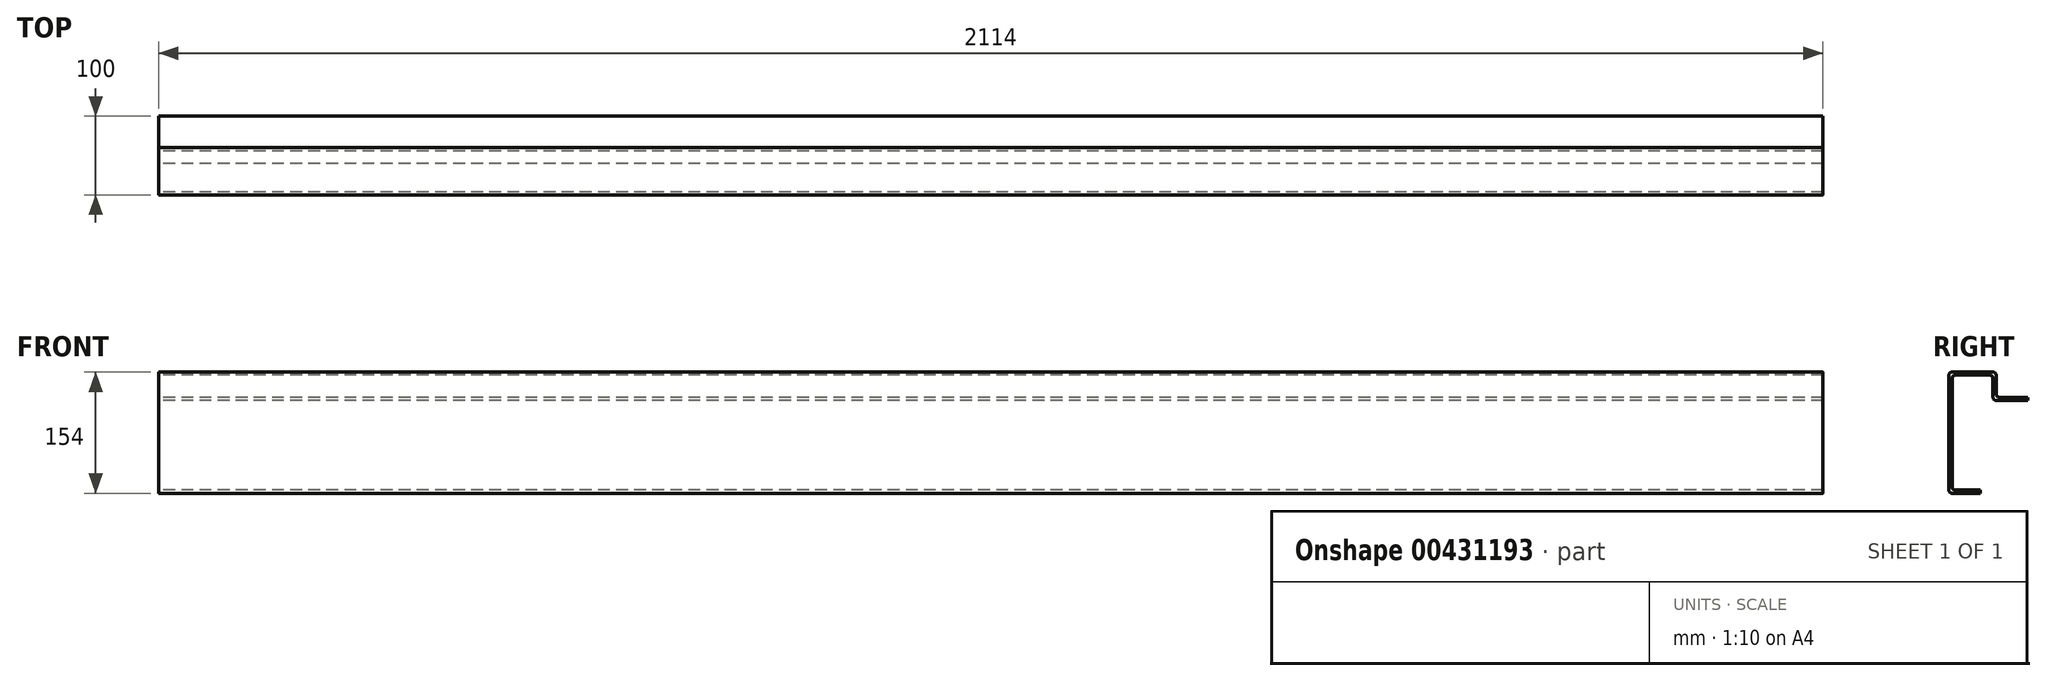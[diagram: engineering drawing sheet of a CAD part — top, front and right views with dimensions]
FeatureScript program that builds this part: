
annotation { "Feature Type Name" : "Feature", "Feature Type Description" : "" }
export const myFeature = defineFeature(function(context is Context, id is Id, definition is map)
    precondition{}
    {
        {
            var Q0;
            Q0=qCreatedBy(makeId("Right.planeOp"),FACE);
            var sketch = newSketch(context, id + "F0", { "sketchPlane" : qUnion([Q0])});
            skLineSegment(sketch, "E0", {"start": v(4, 0) * mm, "end": v(40, 0) * mm});
            skLineSegment(sketch, "E1", {"start": v(0, 4) * mm, "end": v(0, 150) * mm});
            skLineSegment(sketch, "E2", {"start": v(4, 154) * mm, "end": v(56, 154) * mm});
            skLineSegment(sketch, "E3", {"start": v(60, 154) * mm, "end": v(100, 154) * mm});
            skLineSegment(sketch, "E4", {"start": v(60, 150) * mm, "end": v(60, 126) * mm});
            skLineSegment(sketch, "E5", {"start": v(64, 122) * mm, "end": v(100, 122) * mm});
            skLineSegment(sketch, "E6.0", {"start": v(60, 118) * mm, "end": v(100, 118) * mm});
            skLineSegment(sketch, "E7.0", {"start": v(56, 146) * mm, "end": v(56, 122) * mm});
            skLineSegment(sketch, "E8.0", {"start": v(8, 150) * mm, "end": v(52, 150) * mm});
            skLineSegment(sketch, "E9.0", {"start": v(4, 8) * mm, "end": v(4, 146) * mm});
            skLineSegment(sketch, "E10.0", {"start": v(8, 4) * mm, "end": v(40, 4) * mm});
            skLineSegment(sketch, "E11", {"start": v(40, 4) * mm, "end": v(40, 0) * mm});
            skLineSegment(sketch, "E12", {"start": v(100, 122) * mm, "end": v(100, 118) * mm});
            skPoint(sketch, "E13.visualSharp", {"position": v(0, 154) * mm});
            skArc(sketch, "E13.filletArc", {"start": v(4, 154) * mm, "mid": v(1.17, 152.83) * mm, "end": v(0, 150) * mm});
            skArc(sketch, "E14.filletArc", {"start": v(8, 150) * mm, "mid": v(5.17, 148.83) * mm, "end": v(4, 146) * mm});
            skPoint(sketch, "E15.visualSharp", {"position": v(56, 150) * mm});
            skArc(sketch, "E15.filletArc", {"start": v(56, 146) * mm, "mid": v(54.83, 148.83) * mm, "end": v(52, 150) * mm});
            skPoint(sketch, "E16.visualSharp", {"position": v(60, 154) * mm});
            skArc(sketch, "E16.filletArc", {"start": v(60, 150) * mm, "mid": v(58.83, 152.83) * mm, "end": v(56, 154) * mm});
            skPoint(sketch, "E17.visualSharp", {"position": v(60, 122) * mm});
            skArc(sketch, "E17.filletArc", {"start": v(60, 126) * mm, "mid": v(61.17, 123.17) * mm, "end": v(64, 122) * mm});
            skPoint(sketch, "E18.visualSharp", {"position": v(56, 118) * mm});
            skArc(sketch, "E18.filletArc", {"start": v(56, 122) * mm, "mid": v(57.17, 119.17) * mm, "end": v(60, 118) * mm});
            skPoint(sketch, "E19.visualSharp", {"position": v(4, 4) * mm});
            skArc(sketch, "E19.filletArc", {"start": v(4, 8) * mm, "mid": v(5.17, 5.17) * mm, "end": v(8, 4) * mm});
            skPoint(sketch, "E20.visualSharp", {"position": v(0, 0) * mm});
            skArc(sketch, "E20.filletArc", {"start": v(0, 4) * mm, "mid": v(1.17, 1.17) * mm, "end": v(4, 0) * mm});
            skSolve(sketch);
        }
        {
            var Q0;
            Q0=makeQuery(id+"F0.imprint","IMPRINT",FACE,{"disambiguationData":[TD([[makeQuery(id+"F0.imprint","IMPRINT",EDGE,{"derivedFrom":sQuery(id+"F0.wireOp",EDGE,"E0")}),1.0]])]});
            extrude(context, id + "F1", {"entities" : qUnion([Q0]), "depth" : 2114 * mm});
        }
    });
